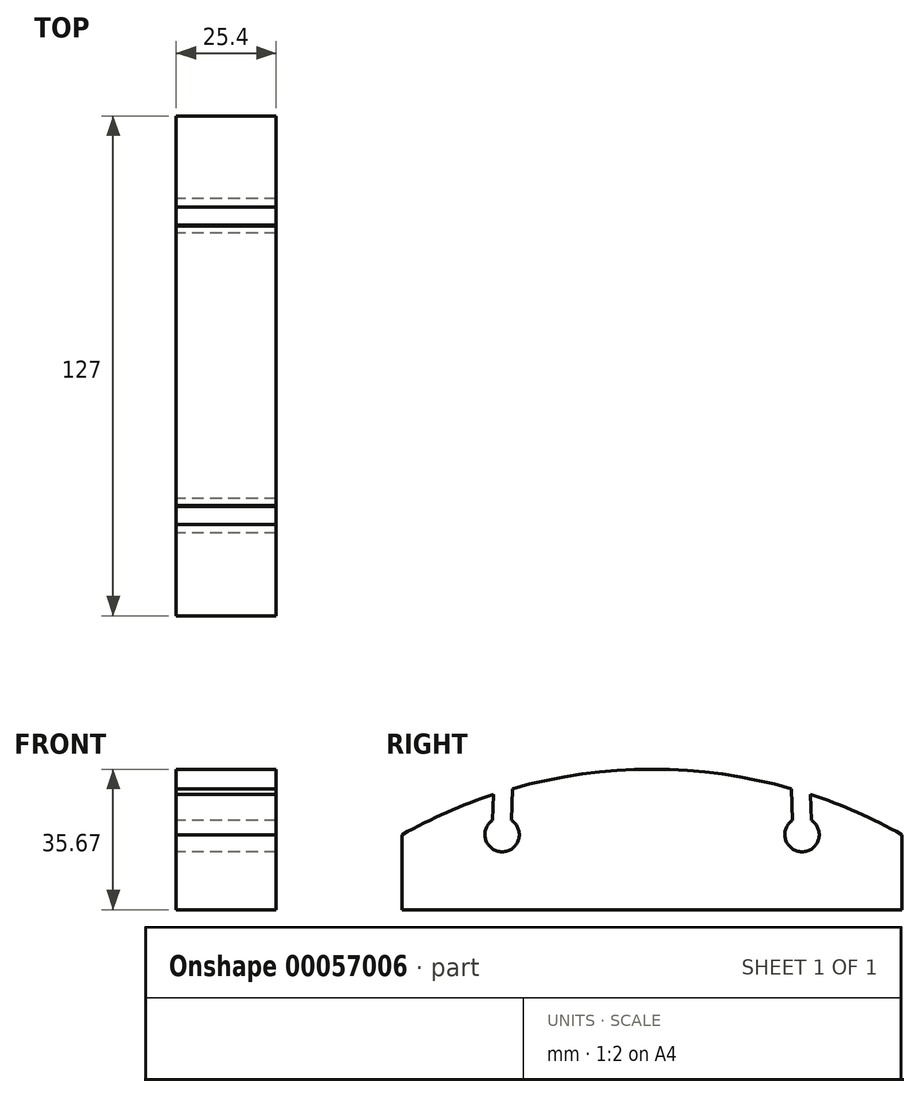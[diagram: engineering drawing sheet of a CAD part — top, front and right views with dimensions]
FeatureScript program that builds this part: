
annotation { "Feature Type Name" : "Feature", "Feature Type Description" : "" }
export const myFeature = defineFeature(function(context is Context, id is Id, definition is map)
    precondition{}
    {
        {
            var Q0;
            Q0=qCreatedBy(makeId("Right.planeOp"),FACE);
            var sketch = newSketch(context, id + "F0", { "sketchPlane" : qUnion([Q0])});
            skLineSegment(sketch, "E0.top", {"start": v(-83.42, 20.15) * mm, "end": v(43.58, 20.15) * mm});
            skLineSegment(sketch, "E0.left", {"start": v(-83.42, 39.2) * mm, "end": v(-83.42, 20.15) * mm});
            skLineSegment(sketch, "E0.right", {"start": v(43.58, 39.2) * mm, "end": v(43.58, 20.15) * mm});
            skPoint(sketch, "E1.center.orphan", {"position": v(-76.47, 31.92) * mm});
            skPoint(sketch, "E2.center.orphan", {"position": v(3.37, 31.92) * mm});
            skArc(sketch, "E3", {"start": v(20.35, 49.4) * mm, "mid": v(17.94, 50.17) * mm, "end": v(15.53, 50.88) * mm});
            skPoint(sketch, "E4.end.orphan", {"position": v(14.42, 20.15) * mm});
            skArc(sketch, "E5", {"start": v(15.79, 42.86) * mm, "mid": v(18.18, 34.83) * mm, "end": v(20.56, 42.86) * mm});
            skLineSegment(sketch, "E6.rect.bottom", {"start": v(21.07, 20.15) * mm, "end": v(16.3, 20.15) * mm});
            skLineSegment(sketch, "E7.trimOffspring", {"start": v(15.79, 42.86) * mm, "end": v(15.53, 50.88) * mm});
            skLineSegment(sketch, "E8.trimOffspring", {"start": v(20.56, 42.86) * mm, "end": v(20.35, 49.4) * mm});
            skPoint(sketch, "E6.rect.top.start.orphan", {"position": v(20.06, 58.25) * mm});
            skPoint(sketch, "E9.orphan", {"position": v(15.28, 58.25) * mm});
            skPoint(sketch, "E10.startSnap0", {"position": v(-19.92, 20.15) * mm});
            skPoint(sketch, "E10.endSnap0", {"position": v(-15.56, 55.75) * mm});
            skArc(sketch, "E11.trimOffspring", {"start": v(-15.56, 55.75) * mm, "mid": v(-17.74, 55.8) * mm, "end": v(-19.92, 55.82) * mm});
            skArc(sketch, "E12", {"start": v(43.58, 39.2) * mm, "mid": v(32.21, 44.87) * mm, "end": v(20.35, 49.4) * mm});
            skPoint(sketch, "E10.end.orphan", {"position": v(-15.56, 20.15) * mm});
            skPoint(sketch, "E13.MirrorCS.end.orphan", {"position": v(-51, 50.88) * mm});
            skPoint(sketch, "E13.MirrorCS.start.orphan", {"position": v(-51.27, 42.86) * mm});
            skPoint(sketch, "E14.MirrorCS.end.orphan", {"position": v(-55.83, 49.4) * mm});
            skPoint(sketch, "E14.MirrorCS.start.orphan", {"position": v(-56.05, 42.86) * mm});
            skPoint(sketch, "E15.end.orphan", {"position": v(-17.74, 20.15) * mm});
            skPoint(sketch, "E15.start.orphan", {"position": v(-17.74, 55.8) * mm});
            skArc(sketch, "E16.MirrorCS", {"start": v(-55.64, 42.86) * mm, "mid": v(-58.02, 34.83) * mm, "end": v(-60.41, 42.86) * mm});
            skLineSegment(sketch, "E17.MirrorCS", {"start": v(-55.64, 42.86) * mm, "end": v(-55.37, 50.88) * mm});
            skLineSegment(sketch, "E18.MirrorCS", {"start": v(-60.41, 42.86) * mm, "end": v(-60.2, 49.4) * mm});
            skArc(sketch, "E19.trimOffspring", {"start": v(-60.2, 49.4) * mm, "mid": v(-72.06, 44.87) * mm, "end": v(-83.42, 39.2) * mm});
            skArc(sketch, "E20.trimOffspring", {"start": v(15.53, 50.88) * mm, "mid": v(-19.92, 55.82) * mm, "end": v(-55.37, 50.88) * mm});
            skSolve(sketch);
        }
        {
            var Q0;
            {var subQ1=sQuery(id+"F0.wireOp",EDGE,"E0.left");Q0=makeQuery(id+"F0.imprint","IMPRINT",FACE,{"disambiguationData":[TD([[makeQuery(id+"F0.imprint","IMPRINT",EDGE,{"derivedFrom":subQ1}),1.0]])]});}
            extrude(context, id + "F1", {"entities" : qUnion([Q0]), "depth" : 25.4 * mm});
        }
    });
